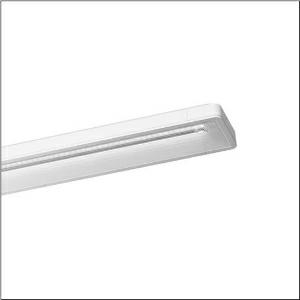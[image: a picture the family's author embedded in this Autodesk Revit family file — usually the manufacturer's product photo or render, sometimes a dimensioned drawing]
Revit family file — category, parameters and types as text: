
# Revit family: taris_r__21_5mt217d04wd_6a0b
name_source: partatom
category: Lighting Fixtures
units: mm (PartAtom-declared; Revit-internal decimal feet)

## family parameters
Cut with Voids When Loaded = No
Host = Face
Light Source = No
Part Type = Normal
Room Calculation Point = No
Round Connector Dimension = Use Diameter
Shared = No

## types (1)
- --- (1 x LED, 6140 lm, 36 W, 4000K)
    Apparent Load = 36 VA
    CIE Flux Codes = 73 96 99 100 100
    Color Rendering = 80
    Color Temperature = 4000K
    Default Elevation = 1800 mm
    Description = Taris® 21, office luminaire, primary anti-glare with micro louvre, primary optical cover: axial lens, of PMMA, structured, CAT 2 (L<= 1500cd/m²), light emission: direct distribution, primary light characteristic: symmetric, installation type: surface-mounted, LED rated luminous flux: 6.140 lm, light colour: 840, colour temperature: 4000K, control gear: ECG DALI, with terminal, 5-pole, mains connection: 230V, AC, 50Hz, rated input power: 36W, housing, luminaire housing, of plastic, traffic white (RAL 9016), length: 1.510 mm, width: 134 mm, height: 50mm, protection rating (complete): IP20, insulation class (complete): insulation class I (protective earthing), certification: CE, ENEC, VDE, protection symbol: F, impact resistance: IK02, permissible ambient temperature for indoor applications: 0..+35°C, standard: EN 50419, packaging unit: 1 piece
    Height = 51 mm
    Lamp = 1 x LED
    Lamp Light Flux = 6140 lm
    Lamp Power = 36 W
    Lamp count = 1
    Length = 1514 mm
    Luminous efficacy = 171 lm/W
    Manufacturer = Siteco
    ModVariant = No
    Model = 5MT217D04WD
    Mounting Place = Ceiling
    Mounting Type = Surface mounted
    Number of Poles = 1
    OnlyDefault = Yes
    Power Factor = 1
    Product Name = Taris® 21
    Product group = office luminaire | ceiling mounted
    ProductGroupID = 302
    Protection Class = Protection class I
    Protection Degree = IP 20
    RLX_Detail_Level = 1
    RlxData = <blob elided: 42673 chars, md5=56a595a5>
    Socket = socket
    Standby Power = 0 W
    System Light Flux = 6140 lm
    System Power = 36 W
    Type Comments = factory setting: luminous flux: 100 % | dim-lin: 254 | 200 mA
    Type Image = l_1004728.jpg
    URL = http://relux.com
    VarID = @adj_129933
    Voltage = 0 V
    Weight = 0.00 kg
    Width = 134 mm

## geometry (parser evidence)
native form markers: Blend x4, Sweep x10
no freeform markers — native parametric forms only
